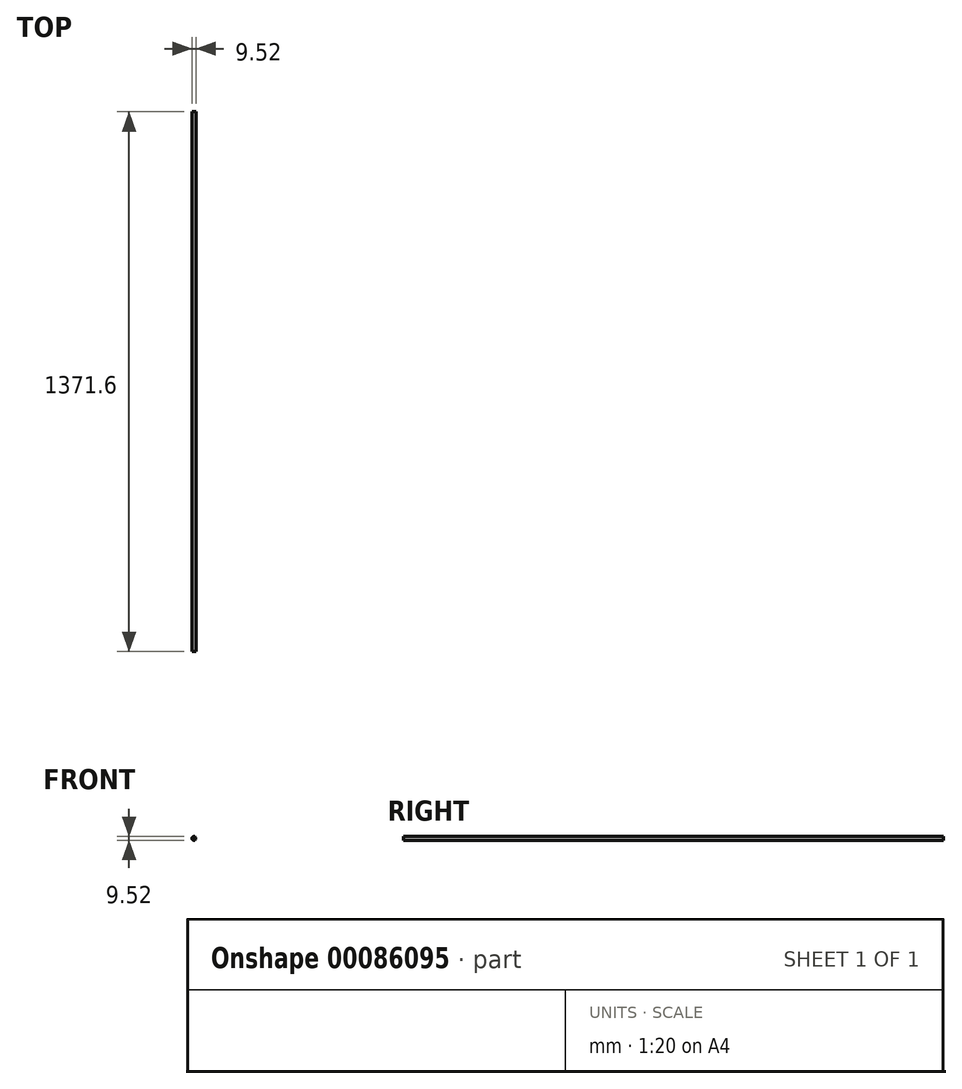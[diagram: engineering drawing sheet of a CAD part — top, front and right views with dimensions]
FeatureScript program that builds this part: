
annotation { "Feature Type Name" : "Feature", "Feature Type Description" : "" }
export const myFeature = defineFeature(function(context is Context, id is Id, definition is map)
    precondition{}
    {
        {
            var Q0;
            Q0=qCreatedBy(makeId("Front.planeOp"),FACE);
            var sketch = newSketch(context, id + "F0", { "sketchPlane" : qUnion([Q0])});
            skCircle(sketch, "E0", {"center": v(0, 0) * mm, "radius": 4.76 * mm});
            skSolve(sketch);
        }
        {
            var Q0;
            Q0 = qSketchRegion(id + "F0", true);
            extrude(context, id + "F1", {"entities" : qUnion([Q0]), "endBound" : BoundingType.SYMMETRIC, "depth" : 1371.6 * mm});
        }
    });
